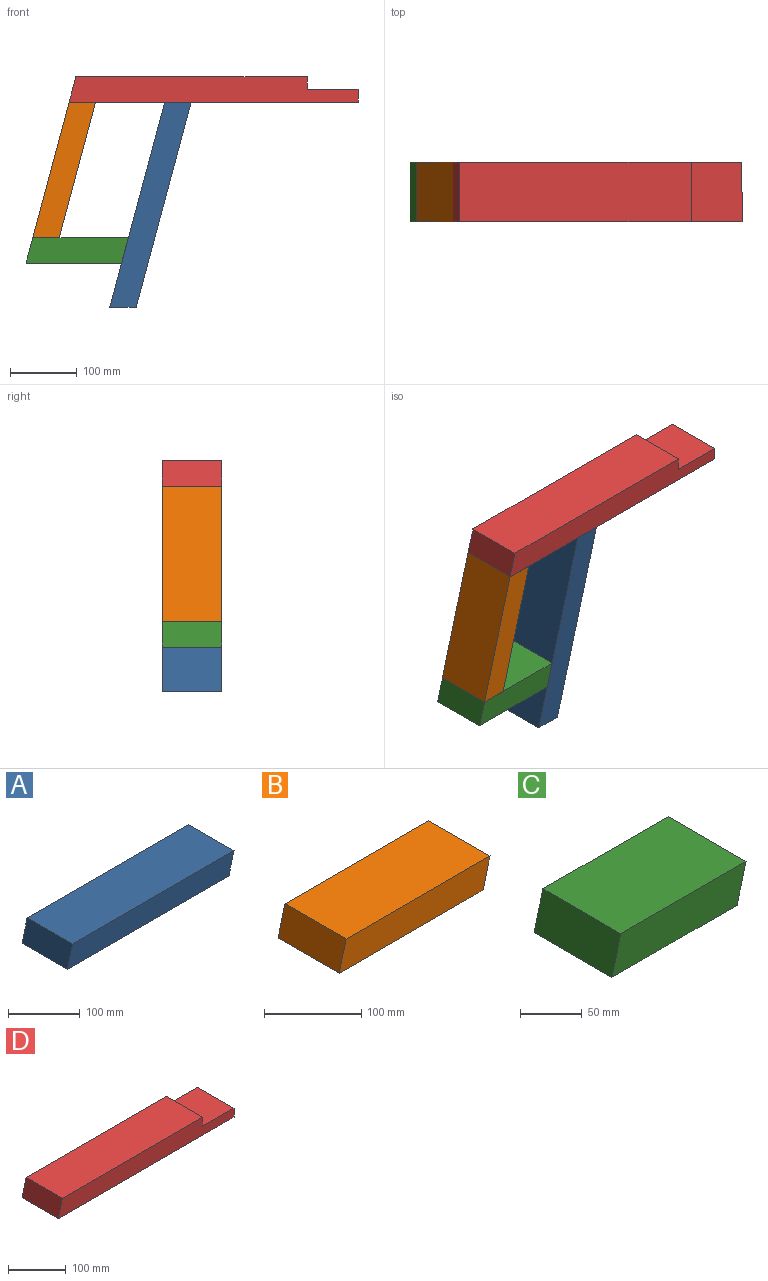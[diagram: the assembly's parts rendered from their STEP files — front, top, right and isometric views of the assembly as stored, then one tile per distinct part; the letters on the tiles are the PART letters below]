
ASSEMBLY  parts=4 mates=3
PART A: 6 faces, bbox 327.7x88.9x38.1 mm
  f0: plane 88.9x38.1mm, normal (-0.97,0,0.26), area 3506.6mm2, adj f1,f3,f4,f5
  f1: plane 317.5x88.9mm, normal (0,0,-1), area 28225.8mm2, adj f0,f2,f4,f5
  f2: plane 88.9x38.1mm, normal (0.97,0,-0.26), area 3506.6mm2, adj f1,f3,f4,f5
  f3: plane 317.5x88.9mm, normal (0,0,1), area 28225.8mm2, adj f0,f2,f4,f5
  f4: plane 327.71x38.1mm, normal (0,-1,0), area 12096.7mm2, adj f0,f1,f2,f3
  f5: plane 327.71x38.1mm, normal (0,1,0), area 12096.7mm2, adj f0,f1,f2,f3
PART B: 6 faces, bbox 219.8x88.9x38.1 mm
  f0: plane 88.9x38.1mm, normal (-0.97,0,0.26), area 3506.6mm2, adj f1,f3,f4,f5
  f1: plane 209.55x88.9mm, normal (0,0,-1), area 18629mm2, adj f0,f2,f4,f5
  f2: plane 88.9x38.1mm, normal (0.97,0,-0.26), area 3506.6mm2, adj f1,f3,f4,f5
  f3: plane 209.55x88.9mm, normal (0,0,1), area 18629mm2, adj f0,f2,f4,f5
  f4: plane 219.76x38.1mm, normal (0,-1,0), area 7983.9mm2, adj f0,f1,f2,f3
  f5: plane 219.76x38.1mm, normal (0,1,0), area 7983.9mm2, adj f0,f1,f2,f3
PART C: 6 faces, bbox 153.1x88.9x38.1 mm
  f0: plane 88.9x38.1mm, normal (-0.97,0,0.26), area 3506.6mm2, adj f1,f3,f4,f5
  f1: plane 142.88x88.9mm, normal (0,0,-1), area 12701.6mm2, adj f0,f2,f4,f5
  f2: plane 88.9x38.1mm, normal (0.97,0,-0.26), area 3506.6mm2, adj f1,f3,f4,f5
  f3: plane 142.88x88.9mm, normal (0,0,1), area 12701.6mm2, adj f0,f2,f4,f5
  f4: plane 153.08x38.1mm, normal (0,-1,0), area 5443.5mm2, adj f0,f1,f2,f3
  f5: plane 153.08x38.1mm, normal (0,1,0), area 5443.5mm2, adj f0,f1,f2,f3
PART D: 8 faces, bbox 431.8x88.9x38.1 mm
  f0: plane 431.8x38.1mm, normal (0,-1,0), area 14805.5mm2, adj f2,f3,f4,f5,f6,f7
  f1: plane 431.8x38.1mm, normal (0,1,0), area 14805.5mm2, adj f2,f3,f4,f5,f6,f7
  f2: plane 88.9x38.1mm, normal (-0.97,0,0.26), area 3506.6mm2, adj f0,f1,f3,f4
  f3: plane 431.8x88.9mm, normal (0,0,-1), area 38387mm2, adj f0,f1,f2,f6
  f4: plane 345.39x88.9mm, normal (0,0,1), area 30705.3mm2, adj f0,f1,f2,f7
  f5: plane 88.9x76.2mm, normal (0,0,1), area 6774.2mm2, adj f0,f1,f6,f7
  f6: plane 88.9x19.05mm, normal (1,0,0), area 1693.5mm2, adj f0,f1,f3,f5
  f7: plane 88.9x19.05mm, normal (1,0,0), area 1693.5mm2, adj f0,f1,f4,f5
PLACE A rot(axis=(-0.79,0,-0.61),180deg) t=(200.76,128.17,-232.01)mm
PLACE B rot(axis=(0.79,0,0.61),180deg) t=(85.83,128.17,-127.73)mm
PLACE C t=(75.62,217.07,-165.83)mm
PLACE D t=(140.06,217.07,74.68)mm
MATE fastened B.f1 <-> D.f2  axis (-0.97,0,0.26) through (140.06,172.62,74.68)mm
MATE fastened D.f3 <-> A.f2  axis (0,0,-1) through (140.06,172.62,74.68)mm
MATE fastened C.f3 <-> B.f0  axis (0,0,1) through (85.83,172.62,-127.73)mm
